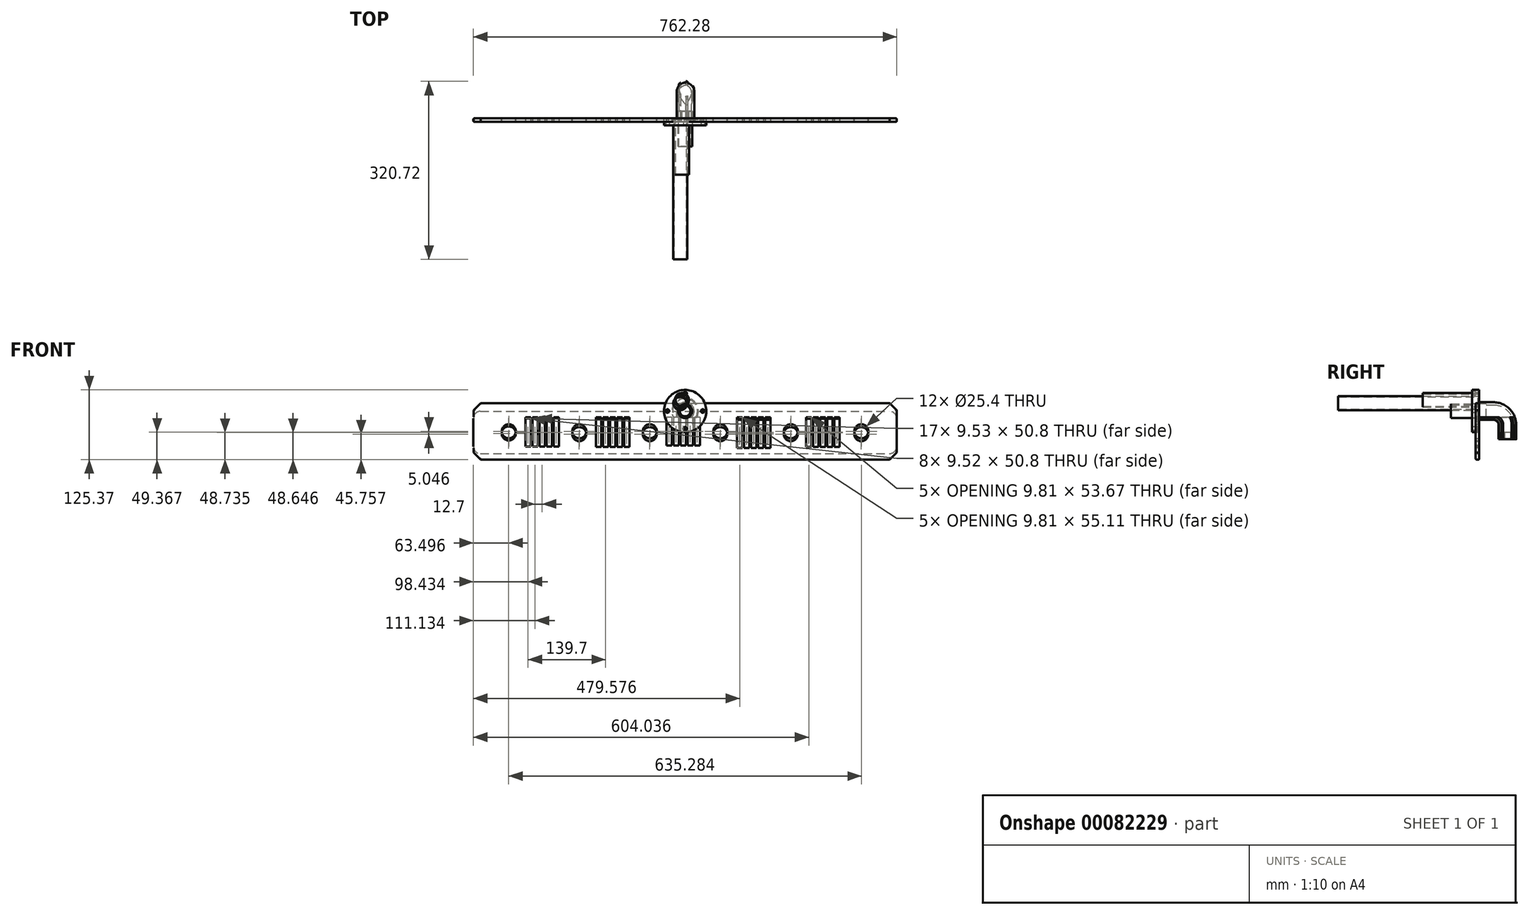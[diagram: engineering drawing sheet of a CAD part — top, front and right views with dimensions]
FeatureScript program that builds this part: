
annotation { "Feature Type Name" : "Feature", "Feature Type Description" : "" }
export const myFeature = defineFeature(function(context is Context, id is Id, definition is map)
    precondition{}
    {
        {
            var Q0;
            Q0=qCreatedBy(makeId("Front.planeOp"),FACE);
            var sketch = newSketch(context, id + "F0", { "sketchPlane" : qUnion([Q0])});
            skCircle(sketch, "E0", {"center": v(0, 0) * mm, "radius": 38.1 * mm});
            skCircle(sketch, "E1", {"center": v(0, 0) * mm, "radius": 9.53 * mm});
            skSolve(sketch);
        }
        {
            var Q0;
            Q0=makeQuery(id+"F0.imprint","IMPRINT",FACE,{"disambiguationData":[TD([[makeQuery(id+"F0.imprint","IMPRINT",EDGE,{"derivedFrom":sQuery(id+"F0.wireOp",EDGE,"E0")}),1.0]])]});
            extrude(context, id + "F1", {"entities" : qUnion([Q0]), "depth" : 12.7 * mm});
        }
        {
            var Q0;
            Q0=makeQuery(id+"F1.opExtrude","CAP_FACE",FACE,{"disambiguationData":[OSD([sQuery(id+"F0.wireOp",EDGE,"E0"),sQuery(id+"F0.wireOp",EDGE,"E1")])],"isStart":false});
            var sketch = newSketch(context, id + "F2", { "sketchPlane" : qUnion([Q0])});
            skCircle(sketch, "E2", {"center": v(0, 0) * mm, "radius": 12.7 * mm});
            skSolve(sketch);
        }
        {
            var Q0;
            Q0=makeQuery(id+"F2.imprint","IMPRINT",FACE,{"disambiguationData":[TD([[makeQuery(id+"F2.imprint","IMPRINT",EDGE,{"derivedFrom":sQuery(id+"F2.wireOp",EDGE,"E2")}),1.0]])]});
            extrude(context, id + "F3", {"entities" : qUnion([Q0]), "operationType" : NewBodyOperationType.REMOVE, "oppositeDirection" : true, "depth" : 6.35 * mm});
        }
        {
            var Q0;
            Q0=makeQuery(id+"F1.opExtrude","CAP_FACE",FACE,{"disambiguationData":[OSD([sQuery(id+"F0.wireOp",EDGE,"E0"),sQuery(id+"F0.wireOp",EDGE,"E1")])],"isStart":false});
            var sketch = newSketch(context, id + "F4", { "sketchPlane" : qUnion([Q0])});
            skPoint(sketch, "E3", {"position": v(0, 31.75) * mm});
            skPoint(sketch, "E4", {"position": v(31.75, 0) * mm});
            skPoint(sketch, "E5", {"position": v(0, -31.75) * mm});
            skPoint(sketch, "E6", {"position": v(-31.75, 0) * mm});
            skSolve(sketch);
        }
        {
            var Q0;
            Q0=sQuery(id+"F4.wireOp",VERTEX,"E3");
            var Q1;
            Q1=sQuery(id+"F4.wireOp",VERTEX,"E6");
            var Q2;
            Q2=sQuery(id+"F4.wireOp",VERTEX,"E4");
            var Q3;
            Q3=sQuery(id+"F4.wireOp",VERTEX,"E5");
            var Q4;
            Q4=makeQuery(id+"F1.opExtrude","SWEPT_BODY",BODY,{"disambiguationData":[OSD([sQuery(id+"F0.wireOp",EDGE,"E0"),sQuery(id+"F0.wireOp",EDGE,"E1")])]});
            hole(context, id + "F5", {"style" : HoleStyle.C_BORE, "endStyle" : HoleEndStyle.THROUGH, "holeDiameter" : 3.17 * mm, "cBoreDiameter" : 6.35 * mm, "cBoreDepth" : 6.35 * mm, "locations" : qUnion([Q0, Q1, Q2, Q3]), "scope" : qUnion([Q4]), "isTappedThrough" : true});
        }
        {
            var Q0;
            Q0=makeQuery(id+"F1.opExtrude","CAP_FACE",FACE,{"disambiguationData":[OSD([sQuery(id+"F0.wireOp",EDGE,"E0"),sQuery(id+"F0.wireOp",EDGE,"E1")])],"isStart":true});
            var sketch = newSketch(context, id + "F6", { "sketchPlane" : qUnion([Q0])});
            skCircle(sketch, "E7", {"center": v(0, 0) * mm, "radius": 22.23 * mm});
            skCircle(sketch, "E8", {"center": v(0, 0) * mm, "radius": 23.81 * mm});
            skSolve(sketch);
        }
        {
            var Q0;
            Q0=makeQuery(id+"F6.imprint","IMPRINT",FACE,{"disambiguationData":[TD([[makeQuery(id+"F6.imprint","IMPRINT",EDGE,{"derivedFrom":sQuery(id+"F6.wireOp",EDGE,"E7")}),-1.0]])]});
            extrude(context, id + "F7", {"entities" : qUnion([Q0]), "operationType" : NewBodyOperationType.REMOVE, "oppositeDirection" : true, "depth" : 1.9 * mm});
        }
        {
            var Q0;
            Q0=qCreatedBy(makeId("Front.planeOp"),FACE);
            var sketch = newSketch(context, id + "F8", { "sketchPlane" : qUnion([Q0])});
            skCircle(sketch, "E9", {"center": v(0, 0) * mm, "radius": 11.11 * mm});
            skCircle(sketch, "E10", {"center": v(0, 0) * mm, "radius": 12.7 * mm});
            skSolve(sketch);
        }
        {
            var Q0;
            Q0=makeQuery(id+"F8.imprint","IMPRINT",FACE,{"disambiguationData":[TD([[makeQuery(id+"F8.imprint","IMPRINT",EDGE,{"derivedFrom":sQuery(id+"F8.wireOp",EDGE,"E9")}),-1.0]])]});
            extrude(context, id + "F9", {"entities" : qUnion([Q0]), "depth" : 50.8 * mm});
        }
        {
            var Q0;
            Q0=qCreatedBy(makeId("Front.planeOp"),FACE);
            var sketch = newSketch(context, id + "F10", { "sketchPlane" : qUnion([Q0])});
            skCircle(sketch, "E11", {"center": v(-5.87, 19.79) * mm, "radius": 11.11 * mm});
            skCircle(sketch, "E12", {"center": v(-5.87, 19.79) * mm, "radius": 12.7 * mm});
            skSolve(sketch);
        }
        {
            var Q0;
            Q0=makeQuery(id+"F10.imprint","IMPRINT",FACE,{"disambiguationData":[TD([[makeQuery(id+"F10.imprint","IMPRINT",EDGE,{"derivedFrom":sQuery(id+"F10.wireOp",EDGE,"E11")}),-1.0]])]});
            extrude(context, id + "F11", {"entities" : qUnion([Q0]), "depth" : 101.6 * mm});
        }
        {
            var Q0;
            Q0=qCreatedBy(makeId("Front.planeOp"),FACE);
            var sketch = newSketch(context, id + "F12", { "sketchPlane" : qUnion([Q0])});
            skCircle(sketch, "E13", {"center": v(-8.71, 14.3) * mm, "radius": 11.11 * mm});
            skCircle(sketch, "E14", {"center": v(-8.71, 14.3) * mm, "radius": 12.7 * mm});
            skSolve(sketch);
        }
        {
            var Q0;
            Q0=makeQuery(id+"F12.imprint","IMPRINT",FACE,{"disambiguationData":[TD([[makeQuery(id+"F12.imprint","IMPRINT",EDGE,{"derivedFrom":sQuery(id+"F12.wireOp",EDGE,"E13")}),-1.0]])]});
            extrude(context, id + "F13", {"entities" : qUnion([Q0]), "depth" : 254 * mm});
        }
        {
            var Q0;
            Q0=qCreatedBy(makeId("Front.planeOp"),FACE);
            var sketch = newSketch(context, id + "F14", { "sketchPlane" : qUnion([Q0])});
            skCircle(sketch, "E15", {"center": v(0.38, 0.1) * mm, "radius": 11.11 * mm});
            skCircle(sketch, "E16", {"center": v(0.38, 0.1) * mm, "radius": 15.88 * mm});
            skSolve(sketch);
        }
        {
            var Q0;
            Q0=qCreatedBy(makeId("Right.planeOp"),FACE);
            var sketch = newSketch(context, id + "F15", { "sketchPlane" : qUnion([Q0])});
            skLineSegment(sketch, "E17", {"start": v(0, 0) * mm, "end": v(25.4, 0) * mm});
            skLineSegment(sketch, "E18", {"start": v(50.8, -25.4) * mm, "end": v(50.8, -50.8) * mm});
            skPoint(sketch, "E19.visualSharp", {"position": v(50.8, 0) * mm});
            skArc(sketch, "E19.filletArc", {"start": v(50.8, -25.4) * mm, "mid": v(43.36, -7.44) * mm, "end": v(25.4, 0) * mm});
            skSolve(sketch);
        }
        {
            var Q0;
            Q0=makeQuery(id+"F14.imprint","IMPRINT",FACE,{"disambiguationData":[TD([[makeQuery(id+"F14.imprint","IMPRINT",EDGE,{"derivedFrom":sQuery(id+"F14.wireOp",EDGE,"E15")}),-1.0]])]});
            var Q1;
            Q1=sQuery(id+"F15.wireOp",EDGE,"E19.filletArc");
            var Q2;
            Q2=sQuery(id+"F15.wireOp",EDGE,"E17");
            var Q3;
            Q3=sQuery(id+"F15.wireOp",EDGE,"E18");
            sweep(context, id + "F16", {"profiles" : qUnion([Q0]), "path" : qUnion([Q1, Q2, Q3])});
        }
        {
            var Q0;
            Q0=qCreatedBy(makeId("Front.planeOp"),FACE);
            var sketch = newSketch(context, id + "F17", { "sketchPlane" : qUnion([Q0])});
            skCircle(sketch, "E20", {"center": v(0, 0) * mm, "radius": 12.7 * mm});
            skSolve(sketch);
        }
        {
            var Q0;
            Q0=makeQuery(id+"F17.imprint","IMPRINT",FACE,{"disambiguationData":[TD([[makeQuery(id+"F17.imprint","IMPRINT",EDGE,{"derivedFrom":sQuery(id+"F17.wireOp",EDGE,"E20")}),1.0]])]});
            extrude(context, id + "F18", {"entities" : qUnion([Q0]), "operationType" : NewBodyOperationType.REMOVE, "oppositeDirection" : true, "depth" : 12.7 * mm});
        }
        {
            var Q0;
            Q0=makeQuery(id+"F16.opSweep","CAP_FACE",FACE,{"disambiguationData":[OSD([sQuery(id+"F14.wireOp",EDGE,"E15"),sQuery(id+"F14.wireOp",EDGE,"E16"),sQuery(id+"F15.wireOp",VERTEX,"E18.end")])],"isStart":false});
            var sketch = newSketch(context, id + "F19", { "sketchPlane" : qUnion([Q0])});
            skCircle(sketch, "E21", {"center": v(0.38, -50.9) * mm, "radius": 12.7 * mm});
            skSolve(sketch);
        }
        {
            var Q0;
            Q0 = qSketchRegion(id + "F19", true);
            extrude(context, id + "F20", {"entities" : qUnion([Q0]), "operationType" : NewBodyOperationType.REMOVE, "oppositeDirection" : true, "depth" : 12.7 * mm});
        }
        {
            var Q0;
            Q0=qCreatedBy(makeId("Front.planeOp"),FACE);
            var sketch = newSketch(context, id + "F21", { "sketchPlane" : qUnion([Q0])});
            skLineSegment(sketch, "E22.bottom", {"start": v(-381, 14.33) * mm, "end": v(381, 14.33) * mm});
            skLineSegment(sketch, "E22.top", {"start": v(-381, -87.27) * mm, "end": v(381, -87.27) * mm});
            skLineSegment(sketch, "E22.left", {"start": v(-381, 14.33) * mm, "end": v(-381, -87.27) * mm});
            skLineSegment(sketch, "E22.right", {"start": v(381, 14.33) * mm, "end": v(381, -87.27) * mm});
            skCircle(sketch, "E23", {"center": v(-317.5, -36.47) * mm, "radius": 12.7 * mm});
            skPoint(sketch, "E23.centerSnap0", {"position": v(-381, -36.47) * mm});
            skCircle(sketch, "E24", {"center": v(-190.5, -36.47) * mm, "radius": 12.7 * mm});
            skCircle(sketch, "E25", {"center": v(-63.5, -36.47) * mm, "radius": 12.7 * mm});
            skCircle(sketch, "E26", {"center": v(63.5, -36.47) * mm, "radius": 12.7 * mm});
            skCircle(sketch, "E27", {"center": v(190.5, -36.47) * mm, "radius": 12.7 * mm});
            skCircle(sketch, "E28", {"center": v(317.5, -36.47) * mm, "radius": 12.7 * mm});
            skSolve(sketch);
        }
        {
            var Q0;
            Q0=makeQuery(id+"F21.imprint","IMPRINT",FACE,{"disambiguationData":[TD([[makeQuery(id+"F21.imprint","IMPRINT",EDGE,{"derivedFrom":sQuery(id+"F21.wireOp",EDGE,"E22.bottom")}),-1.0]])]});
            extrude(context, id + "F22", {"entities" : qUnion([Q0]), "depth" : 6.35 * mm});
        }
        {
            var Q0;
            Q0=makeQuery(id+"F22.opExtrude","CAP_FACE",FACE,{"disambiguationData":[OSD([sQuery(id+"F21.wireOp",EDGE,"E22.bottom"),sQuery(id+"F21.wireOp",EDGE,"E22.top"),sQuery(id+"F21.wireOp",EDGE,"E22.left"),sQuery(id+"F21.wireOp",EDGE,"E22.right"),sQuery(id+"F21.wireOp",EDGE,"E23"),sQuery(id+"F21.wireOp",EDGE,"E24"),sQuery(id+"F21.wireOp",EDGE,"E25"),sQuery(id+"F21.wireOp",EDGE,"E26"),sQuery(id+"F21.wireOp",EDGE,"E27"),sQuery(id+"F21.wireOp",EDGE,"E28")])],"isStart":false});
            var sketch = newSketch(context, id + "F23", { "sketchPlane" : qUnion([Q0])});
            skLineSegment(sketch, "E29.bottom", {"start": v(-287.32, -11.07) * mm, "end": v(-277.8, -11.07) * mm});
            skLineSegment(sketch, "E29.top", {"start": v(-287.32, -61.87) * mm, "end": v(-277.8, -61.87) * mm});
            skLineSegment(sketch, "E29.left", {"start": v(-287.32, -11.07) * mm, "end": v(-287.32, -61.87) * mm});
            skLineSegment(sketch, "E29.right", {"start": v(-277.8, -11.07) * mm, "end": v(-277.8, -61.87) * mm});
            skLineSegment(sketch, "E30.1.0.0", {"start": v(-274.62, -11.07) * mm, "end": v(-265.1, -11.07) * mm});
            skLineSegment(sketch, "E30.1.0.1", {"start": v(-274.62, -61.87) * mm, "end": v(-265.1, -61.87) * mm});
            skLineSegment(sketch, "E30.1.0.2", {"start": v(-265.1, -11.07) * mm, "end": v(-265.1, -61.87) * mm});
            skLineSegment(sketch, "E30.1.0.3", {"start": v(-274.62, -11.07) * mm, "end": v(-274.62, -61.87) * mm});
            skLineSegment(sketch, "E30.2.0.0", {"start": v(-261.92, -11.07) * mm, "end": v(-252.4, -11.07) * mm});
            skLineSegment(sketch, "E30.2.0.1", {"start": v(-261.92, -61.87) * mm, "end": v(-252.4, -61.87) * mm});
            skLineSegment(sketch, "E30.2.0.2", {"start": v(-252.4, -11.07) * mm, "end": v(-252.4, -61.87) * mm});
            skLineSegment(sketch, "E30.2.0.3", {"start": v(-261.92, -11.07) * mm, "end": v(-261.92, -61.87) * mm});
            skLineSegment(sketch, "E30.3.0.0", {"start": v(-249.22, -11.07) * mm, "end": v(-239.7, -11.07) * mm});
            skLineSegment(sketch, "E30.3.0.1", {"start": v(-249.22, -61.87) * mm, "end": v(-239.7, -61.87) * mm});
            skLineSegment(sketch, "E30.3.0.2", {"start": v(-239.7, -11.07) * mm, "end": v(-239.7, -61.87) * mm});
            skLineSegment(sketch, "E30.3.0.3", {"start": v(-249.22, -11.07) * mm, "end": v(-249.22, -61.87) * mm});
            skLineSegment(sketch, "E30.4.0.0", {"start": v(-236.52, -11.07) * mm, "end": v(-227, -11.07) * mm});
            skLineSegment(sketch, "E30.4.0.1", {"start": v(-236.52, -61.87) * mm, "end": v(-227, -61.87) * mm});
            skLineSegment(sketch, "E30.4.0.2", {"start": v(-227, -11.07) * mm, "end": v(-227, -61.87) * mm});
            skLineSegment(sketch, "E30.4.0.3", {"start": v(-236.52, -11.07) * mm, "end": v(-236.52, -61.87) * mm});
            skLineSegment(sketch, "E30.direction1", {"start": v(-287.32, -11.07) * mm, "end": v(-274.62, -11.07) * mm, "construction": true});
            skLineSegment(sketch, "E31.bottom", {"start": v(-160.32, -11.07) * mm, "end": v(-150.8, -11.07) * mm});
            skLineSegment(sketch, "E31.top", {"start": v(-160.32, -61.87) * mm, "end": v(-150.8, -61.87) * mm});
            skLineSegment(sketch, "E31.left", {"start": v(-160.32, -11.07) * mm, "end": v(-160.32, -61.87) * mm});
            skLineSegment(sketch, "E31.right", {"start": v(-150.8, -11.07) * mm, "end": v(-150.8, -61.87) * mm});
            skLineSegment(sketch, "E32.1.0.0", {"start": v(-147.62, -11.07) * mm, "end": v(-138.1, -11.07) * mm});
            skLineSegment(sketch, "E32.1.0.1", {"start": v(-147.62, -61.87) * mm, "end": v(-138.1, -61.87) * mm});
            skLineSegment(sketch, "E32.1.0.2", {"start": v(-138.1, -11.07) * mm, "end": v(-138.1, -61.87) * mm});
            skLineSegment(sketch, "E32.1.0.3", {"start": v(-147.62, -11.07) * mm, "end": v(-147.62, -61.87) * mm});
            skLineSegment(sketch, "E32.2.0.0", {"start": v(-134.92, -11.07) * mm, "end": v(-125.4, -11.07) * mm});
            skLineSegment(sketch, "E32.2.0.1", {"start": v(-134.92, -61.87) * mm, "end": v(-125.4, -61.87) * mm});
            skLineSegment(sketch, "E32.2.0.2", {"start": v(-125.4, -11.07) * mm, "end": v(-125.4, -61.87) * mm});
            skLineSegment(sketch, "E32.2.0.3", {"start": v(-134.92, -11.07) * mm, "end": v(-134.92, -61.87) * mm});
            skLineSegment(sketch, "E32.3.0.0", {"start": v(-122.22, -11.07) * mm, "end": v(-112.7, -11.07) * mm});
            skLineSegment(sketch, "E32.3.0.1", {"start": v(-122.22, -61.87) * mm, "end": v(-112.7, -61.87) * mm});
            skLineSegment(sketch, "E32.3.0.2", {"start": v(-112.7, -11.07) * mm, "end": v(-112.7, -61.87) * mm});
            skLineSegment(sketch, "E32.3.0.3", {"start": v(-122.22, -11.07) * mm, "end": v(-122.22, -61.87) * mm});
            skLineSegment(sketch, "E32.4.0.0", {"start": v(-109.52, -11.07) * mm, "end": v(-100, -11.07) * mm});
            skLineSegment(sketch, "E32.4.0.1", {"start": v(-109.52, -61.87) * mm, "end": v(-100, -61.87) * mm});
            skLineSegment(sketch, "E32.4.0.2", {"start": v(-100, -11.07) * mm, "end": v(-100, -61.87) * mm});
            skLineSegment(sketch, "E32.4.0.3", {"start": v(-109.52, -11.07) * mm, "end": v(-109.52, -61.87) * mm});
            skLineSegment(sketch, "E32.direction1", {"start": v(-160.32, -11.07) * mm, "end": v(-147.62, -11.07) * mm, "construction": true});
            skLineSegment(sketch, "E33.bottom", {"start": v(-33.32, -11.07) * mm, "end": v(-23.8, -11.07) * mm});
            skLineSegment(sketch, "E33.top", {"start": v(-33.32, -61.87) * mm, "end": v(-23.8, -61.87) * mm});
            skLineSegment(sketch, "E33.left", {"start": v(-33.32, -11.07) * mm, "end": v(-33.32, -61.87) * mm});
            skLineSegment(sketch, "E33.right", {"start": v(-23.8, -11.07) * mm, "end": v(-23.8, -61.87) * mm});
            skLineSegment(sketch, "E34.1.0.0", {"start": v(-20.62, -11.07) * mm, "end": v(-11.1, -11.07) * mm});
            skLineSegment(sketch, "E34.1.0.1", {"start": v(-20.62, -61.87) * mm, "end": v(-11.1, -61.87) * mm});
            skLineSegment(sketch, "E34.1.0.2", {"start": v(-11.1, -11.07) * mm, "end": v(-11.1, -61.87) * mm});
            skLineSegment(sketch, "E34.1.0.3", {"start": v(-20.62, -11.07) * mm, "end": v(-20.62, -61.87) * mm});
            skLineSegment(sketch, "E34.2.0.0", {"start": v(-7.92, -11.07) * mm, "end": v(1.6, -11.07) * mm});
            skLineSegment(sketch, "E34.2.0.1", {"start": v(-7.92, -61.87) * mm, "end": v(1.6, -61.87) * mm});
            skLineSegment(sketch, "E34.2.0.2", {"start": v(1.6, -11.07) * mm, "end": v(1.6, -61.87) * mm});
            skLineSegment(sketch, "E34.2.0.3", {"start": v(-7.92, -11.07) * mm, "end": v(-7.92, -61.87) * mm});
            skLineSegment(sketch, "E34.3.0.0", {"start": v(4.78, -11.07) * mm, "end": v(14.3, -11.07) * mm});
            skLineSegment(sketch, "E34.3.0.1", {"start": v(4.78, -61.87) * mm, "end": v(14.3, -61.87) * mm});
            skLineSegment(sketch, "E34.3.0.2", {"start": v(14.3, -11.07) * mm, "end": v(14.3, -61.87) * mm});
            skLineSegment(sketch, "E34.3.0.3", {"start": v(4.78, -11.07) * mm, "end": v(4.78, -61.87) * mm});
            skLineSegment(sketch, "E34.4.0.0", {"start": v(17.48, -11.07) * mm, "end": v(27, -11.07) * mm});
            skLineSegment(sketch, "E34.4.0.1", {"start": v(17.48, -61.87) * mm, "end": v(27, -61.87) * mm});
            skLineSegment(sketch, "E34.4.0.2", {"start": v(27, -11.07) * mm, "end": v(27, -61.87) * mm});
            skLineSegment(sketch, "E34.4.0.3", {"start": v(17.48, -11.07) * mm, "end": v(17.48, -61.87) * mm});
            skLineSegment(sketch, "E34.direction1", {"start": v(-33.32, -11.07) * mm, "end": v(-20.62, -11.07) * mm, "construction": true});
            skLineSegment(sketch, "E35.bottom", {"start": v(93.68, -11.07) * mm, "end": v(103.2, -11.07) * mm});
            skLineSegment(sketch, "E35.top", {"start": v(93.68, -61.87) * mm, "end": v(103.2, -61.87) * mm});
            skLineSegment(sketch, "E35.left", {"start": v(93.68, -11.07) * mm, "end": v(93.68, -61.87) * mm});
            skLineSegment(sketch, "E35.right", {"start": v(103.2, -11.07) * mm, "end": v(103.2, -61.87) * mm});
            skLineSegment(sketch, "E36.1.0.0", {"start": v(106.38, -11.07) * mm, "end": v(115.9, -11.07) * mm});
            skLineSegment(sketch, "E36.1.0.1", {"start": v(106.38, -61.87) * mm, "end": v(115.9, -61.87) * mm});
            skLineSegment(sketch, "E36.1.0.2", {"start": v(115.9, -11.07) * mm, "end": v(115.9, -61.87) * mm});
            skLineSegment(sketch, "E36.1.0.3", {"start": v(106.38, -11.07) * mm, "end": v(106.38, -61.87) * mm});
            skLineSegment(sketch, "E36.2.0.0", {"start": v(119.08, -11.07) * mm, "end": v(128.6, -11.07) * mm});
            skLineSegment(sketch, "E36.2.0.1", {"start": v(119.08, -61.87) * mm, "end": v(128.6, -61.87) * mm});
            skLineSegment(sketch, "E36.2.0.2", {"start": v(128.6, -11.07) * mm, "end": v(128.6, -61.87) * mm});
            skLineSegment(sketch, "E36.2.0.3", {"start": v(119.08, -11.07) * mm, "end": v(119.08, -61.87) * mm});
            skLineSegment(sketch, "E36.3.0.0", {"start": v(131.78, -11.07) * mm, "end": v(141.3, -11.07) * mm});
            skLineSegment(sketch, "E36.3.0.1", {"start": v(131.78, -61.87) * mm, "end": v(141.3, -61.87) * mm});
            skLineSegment(sketch, "E36.3.0.2", {"start": v(141.3, -11.07) * mm, "end": v(141.3, -61.87) * mm});
            skLineSegment(sketch, "E36.3.0.3", {"start": v(131.78, -11.07) * mm, "end": v(131.78, -61.87) * mm});
            skLineSegment(sketch, "E36.4.0.0", {"start": v(144.48, -11.07) * mm, "end": v(154, -11.07) * mm});
            skLineSegment(sketch, "E36.4.0.1", {"start": v(144.48, -61.87) * mm, "end": v(154, -61.87) * mm});
            skLineSegment(sketch, "E36.4.0.2", {"start": v(154, -11.07) * mm, "end": v(154, -61.87) * mm});
            skLineSegment(sketch, "E36.4.0.3", {"start": v(144.48, -11.07) * mm, "end": v(144.48, -61.87) * mm});
            skLineSegment(sketch, "E36.direction1", {"start": v(93.68, -11.07) * mm, "end": v(106.38, -11.07) * mm, "construction": true});
            skLineSegment(sketch, "E37.bottom", {"start": v(218.14, -11.07) * mm, "end": v(227.66, -11.07) * mm});
            skLineSegment(sketch, "E37.top", {"start": v(218.14, -61.87) * mm, "end": v(227.66, -61.87) * mm});
            skLineSegment(sketch, "E37.left", {"start": v(218.14, -11.07) * mm, "end": v(218.14, -61.87) * mm});
            skLineSegment(sketch, "E37.right", {"start": v(227.66, -11.07) * mm, "end": v(227.66, -61.87) * mm});
            skLineSegment(sketch, "E38.1.0.0", {"start": v(230.84, -11.07) * mm, "end": v(240.36, -11.07) * mm});
            skLineSegment(sketch, "E38.1.0.1", {"start": v(230.84, -61.87) * mm, "end": v(240.36, -61.87) * mm});
            skLineSegment(sketch, "E38.1.0.2", {"start": v(240.36, -11.07) * mm, "end": v(240.36, -61.87) * mm});
            skLineSegment(sketch, "E38.1.0.3", {"start": v(230.84, -11.07) * mm, "end": v(230.84, -61.87) * mm});
            skLineSegment(sketch, "E38.2.0.0", {"start": v(243.54, -11.07) * mm, "end": v(253.06, -11.07) * mm});
            skLineSegment(sketch, "E38.2.0.1", {"start": v(243.54, -61.87) * mm, "end": v(253.06, -61.87) * mm});
            skLineSegment(sketch, "E38.2.0.2", {"start": v(253.06, -11.07) * mm, "end": v(253.06, -61.87) * mm});
            skLineSegment(sketch, "E38.2.0.3", {"start": v(243.54, -11.07) * mm, "end": v(243.54, -61.87) * mm});
            skLineSegment(sketch, "E38.3.0.0", {"start": v(256.24, -11.07) * mm, "end": v(265.76, -11.07) * mm});
            skLineSegment(sketch, "E38.3.0.1", {"start": v(256.24, -61.87) * mm, "end": v(265.76, -61.87) * mm});
            skLineSegment(sketch, "E38.3.0.2", {"start": v(265.76, -11.07) * mm, "end": v(265.76, -61.87) * mm});
            skLineSegment(sketch, "E38.3.0.3", {"start": v(256.24, -11.07) * mm, "end": v(256.24, -61.87) * mm});
            skLineSegment(sketch, "E38.4.0.0", {"start": v(268.94, -11.07) * mm, "end": v(278.46, -11.07) * mm});
            skLineSegment(sketch, "E38.4.0.1", {"start": v(268.94, -61.87) * mm, "end": v(278.46, -61.87) * mm});
            skLineSegment(sketch, "E38.4.0.2", {"start": v(278.46, -11.07) * mm, "end": v(278.46, -61.87) * mm});
            skLineSegment(sketch, "E38.4.0.3", {"start": v(268.94, -11.07) * mm, "end": v(268.94, -61.87) * mm});
            skLineSegment(sketch, "E38.direction1", {"start": v(218.14, -11.07) * mm, "end": v(230.84, -11.07) * mm, "construction": true});
            skSolve(sketch);
        }
        {
            var Q0;
            Q0 = qSketchRegion(id + "F23", true);
            extrude(context, id + "F24", {"entities" : qUnion([Q0]), "operationType" : NewBodyOperationType.REMOVE, "endBound" : BoundingType.THROUGH_ALL, "oppositeDirection" : true, "depth" : 25.4 * mm});
        }
        {
            var Q0;
            Q0=makeQuery(id+"F22.opExtrude","SWEPT_EDGE",EDGE,{"disambiguationData":[OSD([sQuery(id+"F21.wireOp",EDGE,"E22.bottom"),sQuery(id+"F21.wireOp",EDGE,"E22.left")])]});
            var Q1;
            Q1=makeQuery(id+"F22.opExtrude","SWEPT_EDGE",EDGE,{"disambiguationData":[OSD([sQuery(id+"F21.wireOp",EDGE,"E22.top"),sQuery(id+"F21.wireOp",EDGE,"E22.left")])]});
            var Q2;
            Q2=makeQuery(id+"F22.opExtrude","SWEPT_EDGE",EDGE,{"disambiguationData":[OSD([sQuery(id+"F21.wireOp",EDGE,"E22.bottom"),sQuery(id+"F21.wireOp",EDGE,"E22.right")])]});
            var Q3;
            Q3=makeQuery(id+"F22.opExtrude","SWEPT_EDGE",EDGE,{"disambiguationData":[OSD([sQuery(id+"F21.wireOp",EDGE,"E22.top"),sQuery(id+"F21.wireOp",EDGE,"E22.right")])]});
            chamfer(context, id + "F25", {"entities" : qUnion([Q0, Q1, Q2, Q3]), "width" : 12.7 * mm, "tangentPropagation" : true});
        }
        {
            var Q0;
            {var subQ0=sQuery(id+"F21.wireOp",EDGE,"E22.left");var subQ1=sQuery(id+"F21.wireOp",EDGE,"E22.bottom");Q0=makeQuery(id+"F25.opChamfer","BLEND_EDGE",EDGE,{"blendedFrom":[makeQuery(id+"F22.opExtrude","SWEPT_EDGE",EDGE,{"disambiguationData":[OSD([subQ1,subQ0])]}),makeQuery(id+"F22.opExtrude","CAP_FACE",FACE,{"disambiguationData":[OSD([subQ1,sQuery(id+"F21.wireOp",EDGE,"E22.top"),subQ0,sQuery(id+"F21.wireOp",EDGE,"E22.right"),sQuery(id+"F21.wireOp",EDGE,"E23"),sQuery(id+"F21.wireOp",EDGE,"E24"),sQuery(id+"F21.wireOp",EDGE,"E25"),sQuery(id+"F21.wireOp",EDGE,"E26"),sQuery(id+"F21.wireOp",EDGE,"E27"),sQuery(id+"F21.wireOp",EDGE,"E28")])],"isStart":false})],"blendedInto":[makeQuery(id+"F22.opExtrude","CAP_FACE",FACE,{"disambiguationData":[OSD([subQ1,sQuery(id+"F21.wireOp",EDGE,"E22.top"),subQ0,sQuery(id+"F21.wireOp",EDGE,"E22.right"),sQuery(id+"F21.wireOp",EDGE,"E23"),sQuery(id+"F21.wireOp",EDGE,"E24"),sQuery(id+"F21.wireOp",EDGE,"E25"),sQuery(id+"F21.wireOp",EDGE,"E26"),sQuery(id+"F21.wireOp",EDGE,"E27"),sQuery(id+"F21.wireOp",EDGE,"E28")])],"isStart":false})]});}
            var Q1;
            {var subQ0=sQuery(id+"F21.wireOp",EDGE,"E22.left");var subQ1=sQuery(id+"F21.wireOp",EDGE,"E22.top");Q1=makeQuery(id+"F25.opChamfer","BLEND_EDGE",EDGE,{"blendedFrom":[makeQuery(id+"F22.opExtrude","SWEPT_EDGE",EDGE,{"disambiguationData":[OSD([subQ1,subQ0])]}),makeQuery(id+"F22.opExtrude","CAP_FACE",FACE,{"disambiguationData":[OSD([sQuery(id+"F21.wireOp",EDGE,"E22.bottom"),subQ1,subQ0,sQuery(id+"F21.wireOp",EDGE,"E22.right"),sQuery(id+"F21.wireOp",EDGE,"E23"),sQuery(id+"F21.wireOp",EDGE,"E24"),sQuery(id+"F21.wireOp",EDGE,"E25"),sQuery(id+"F21.wireOp",EDGE,"E26"),sQuery(id+"F21.wireOp",EDGE,"E27"),sQuery(id+"F21.wireOp",EDGE,"E28")])],"isStart":false})],"blendedInto":[makeQuery(id+"F22.opExtrude","CAP_FACE",FACE,{"disambiguationData":[OSD([sQuery(id+"F21.wireOp",EDGE,"E22.bottom"),subQ1,subQ0,sQuery(id+"F21.wireOp",EDGE,"E22.right"),sQuery(id+"F21.wireOp",EDGE,"E23"),sQuery(id+"F21.wireOp",EDGE,"E24"),sQuery(id+"F21.wireOp",EDGE,"E25"),sQuery(id+"F21.wireOp",EDGE,"E26"),sQuery(id+"F21.wireOp",EDGE,"E27"),sQuery(id+"F21.wireOp",EDGE,"E28")])],"isStart":false})]});}
            var Q2;
            {var subQ0=sQuery(id+"F21.wireOp",EDGE,"E22.right");var subQ1=sQuery(id+"F21.wireOp",EDGE,"E22.bottom");Q2=makeQuery(id+"F25.opChamfer","BLEND_EDGE",EDGE,{"blendedFrom":[makeQuery(id+"F22.opExtrude","SWEPT_EDGE",EDGE,{"disambiguationData":[OSD([subQ1,subQ0])]}),makeQuery(id+"F22.opExtrude","CAP_FACE",FACE,{"disambiguationData":[OSD([subQ1,sQuery(id+"F21.wireOp",EDGE,"E22.top"),sQuery(id+"F21.wireOp",EDGE,"E22.left"),subQ0,sQuery(id+"F21.wireOp",EDGE,"E23"),sQuery(id+"F21.wireOp",EDGE,"E24"),sQuery(id+"F21.wireOp",EDGE,"E25"),sQuery(id+"F21.wireOp",EDGE,"E26"),sQuery(id+"F21.wireOp",EDGE,"E27"),sQuery(id+"F21.wireOp",EDGE,"E28")])],"isStart":false})],"blendedInto":[makeQuery(id+"F22.opExtrude","CAP_FACE",FACE,{"disambiguationData":[OSD([subQ1,sQuery(id+"F21.wireOp",EDGE,"E22.top"),sQuery(id+"F21.wireOp",EDGE,"E22.left"),subQ0,sQuery(id+"F21.wireOp",EDGE,"E23"),sQuery(id+"F21.wireOp",EDGE,"E24"),sQuery(id+"F21.wireOp",EDGE,"E25"),sQuery(id+"F21.wireOp",EDGE,"E26"),sQuery(id+"F21.wireOp",EDGE,"E27"),sQuery(id+"F21.wireOp",EDGE,"E28")])],"isStart":false})]});}
            var Q3;
            {var subQ0=sQuery(id+"F21.wireOp",EDGE,"E22.right");var subQ1=sQuery(id+"F21.wireOp",EDGE,"E22.top");Q3=makeQuery(id+"F25.opChamfer","BLEND_EDGE",EDGE,{"blendedFrom":[makeQuery(id+"F22.opExtrude","SWEPT_EDGE",EDGE,{"disambiguationData":[OSD([subQ1,subQ0])]}),makeQuery(id+"F22.opExtrude","CAP_FACE",FACE,{"disambiguationData":[OSD([sQuery(id+"F21.wireOp",EDGE,"E22.bottom"),subQ1,sQuery(id+"F21.wireOp",EDGE,"E22.left"),subQ0,sQuery(id+"F21.wireOp",EDGE,"E23"),sQuery(id+"F21.wireOp",EDGE,"E24"),sQuery(id+"F21.wireOp",EDGE,"E25"),sQuery(id+"F21.wireOp",EDGE,"E26"),sQuery(id+"F21.wireOp",EDGE,"E27"),sQuery(id+"F21.wireOp",EDGE,"E28")])],"isStart":false})],"blendedInto":[makeQuery(id+"F22.opExtrude","CAP_FACE",FACE,{"disambiguationData":[OSD([sQuery(id+"F21.wireOp",EDGE,"E22.bottom"),subQ1,sQuery(id+"F21.wireOp",EDGE,"E22.left"),subQ0,sQuery(id+"F21.wireOp",EDGE,"E23"),sQuery(id+"F21.wireOp",EDGE,"E24"),sQuery(id+"F21.wireOp",EDGE,"E25"),sQuery(id+"F21.wireOp",EDGE,"E26"),sQuery(id+"F21.wireOp",EDGE,"E27"),sQuery(id+"F21.wireOp",EDGE,"E28")])],"isStart":false})]});}
            var Q4;
            Q4=makeQuery(id+"F22.opExtrude","CAP_EDGE",EDGE,{"disambiguationData":[OSD([sQuery(id+"F21.wireOp",EDGE,"E22.bottom")])],"isStart":false});
            var Q5;
            Q5=makeQuery(id+"F22.opExtrude","CAP_EDGE",EDGE,{"disambiguationData":[OSD([sQuery(id+"F21.wireOp",EDGE,"E22.top")])],"isStart":false});
            var Q6;
            Q6=makeQuery(id+"F22.opExtrude","CAP_EDGE",EDGE,{"disambiguationData":[OSD([sQuery(id+"F21.wireOp",EDGE,"E22.left")])],"isStart":false});
            var Q7;
            Q7=makeQuery(id+"F22.opExtrude","CAP_EDGE",EDGE,{"disambiguationData":[OSD([sQuery(id+"F21.wireOp",EDGE,"E22.right")])],"isStart":false});
            var Q8;
            Q8=makeQuery(id+"F22.opExtrude","CAP_EDGE",EDGE,{"disambiguationData":[OSD([sQuery(id+"F21.wireOp",EDGE,"E22.bottom")])],"isStart":true});
            var Q9;
            {var subQ0=sQuery(id+"F21.wireOp",EDGE,"E22.right");var subQ1=sQuery(id+"F21.wireOp",EDGE,"E22.bottom");Q9=makeQuery(id+"F25.opChamfer","BLEND_EDGE",EDGE,{"blendedFrom":[makeQuery(id+"F22.opExtrude","SWEPT_EDGE",EDGE,{"disambiguationData":[OSD([subQ1,subQ0])]}),makeQuery(id+"F22.opExtrude","CAP_FACE",FACE,{"disambiguationData":[OSD([subQ1,sQuery(id+"F21.wireOp",EDGE,"E22.top"),sQuery(id+"F21.wireOp",EDGE,"E22.left"),subQ0,sQuery(id+"F21.wireOp",EDGE,"E23"),sQuery(id+"F21.wireOp",EDGE,"E24"),sQuery(id+"F21.wireOp",EDGE,"E25"),sQuery(id+"F21.wireOp",EDGE,"E26"),sQuery(id+"F21.wireOp",EDGE,"E27"),sQuery(id+"F21.wireOp",EDGE,"E28")])],"isStart":true})],"blendedInto":[makeQuery(id+"F22.opExtrude","CAP_FACE",FACE,{"disambiguationData":[OSD([subQ1,sQuery(id+"F21.wireOp",EDGE,"E22.top"),sQuery(id+"F21.wireOp",EDGE,"E22.left"),subQ0,sQuery(id+"F21.wireOp",EDGE,"E23"),sQuery(id+"F21.wireOp",EDGE,"E24"),sQuery(id+"F21.wireOp",EDGE,"E25"),sQuery(id+"F21.wireOp",EDGE,"E26"),sQuery(id+"F21.wireOp",EDGE,"E27"),sQuery(id+"F21.wireOp",EDGE,"E28")])],"isStart":true})]});}
            var Q10;
            Q10=makeQuery(id+"F22.opExtrude","CAP_EDGE",EDGE,{"disambiguationData":[OSD([sQuery(id+"F21.wireOp",EDGE,"E22.right")])],"isStart":true});
            var Q11;
            {var subQ0=sQuery(id+"F21.wireOp",EDGE,"E22.right");var subQ1=sQuery(id+"F21.wireOp",EDGE,"E22.top");Q11=makeQuery(id+"F25.opChamfer","BLEND_EDGE",EDGE,{"blendedFrom":[makeQuery(id+"F22.opExtrude","SWEPT_EDGE",EDGE,{"disambiguationData":[OSD([subQ1,subQ0])]}),makeQuery(id+"F22.opExtrude","CAP_FACE",FACE,{"disambiguationData":[OSD([sQuery(id+"F21.wireOp",EDGE,"E22.bottom"),subQ1,sQuery(id+"F21.wireOp",EDGE,"E22.left"),subQ0,sQuery(id+"F21.wireOp",EDGE,"E23"),sQuery(id+"F21.wireOp",EDGE,"E24"),sQuery(id+"F21.wireOp",EDGE,"E25"),sQuery(id+"F21.wireOp",EDGE,"E26"),sQuery(id+"F21.wireOp",EDGE,"E27"),sQuery(id+"F21.wireOp",EDGE,"E28")])],"isStart":true})],"blendedInto":[makeQuery(id+"F22.opExtrude","CAP_FACE",FACE,{"disambiguationData":[OSD([sQuery(id+"F21.wireOp",EDGE,"E22.bottom"),subQ1,sQuery(id+"F21.wireOp",EDGE,"E22.left"),subQ0,sQuery(id+"F21.wireOp",EDGE,"E23"),sQuery(id+"F21.wireOp",EDGE,"E24"),sQuery(id+"F21.wireOp",EDGE,"E25"),sQuery(id+"F21.wireOp",EDGE,"E26"),sQuery(id+"F21.wireOp",EDGE,"E27"),sQuery(id+"F21.wireOp",EDGE,"E28")])],"isStart":true})]});}
            var Q12;
            Q12=makeQuery(id+"F22.opExtrude","CAP_EDGE",EDGE,{"disambiguationData":[OSD([sQuery(id+"F21.wireOp",EDGE,"E22.top")])],"isStart":true});
            var Q13;
            {var subQ0=sQuery(id+"F21.wireOp",EDGE,"E22.left");var subQ1=sQuery(id+"F21.wireOp",EDGE,"E22.bottom");Q13=makeQuery(id+"F25.opChamfer","BLEND_EDGE",EDGE,{"blendedFrom":[makeQuery(id+"F22.opExtrude","SWEPT_EDGE",EDGE,{"disambiguationData":[OSD([subQ1,subQ0])]}),makeQuery(id+"F22.opExtrude","CAP_FACE",FACE,{"disambiguationData":[OSD([subQ1,sQuery(id+"F21.wireOp",EDGE,"E22.top"),subQ0,sQuery(id+"F21.wireOp",EDGE,"E22.right"),sQuery(id+"F21.wireOp",EDGE,"E23"),sQuery(id+"F21.wireOp",EDGE,"E24"),sQuery(id+"F21.wireOp",EDGE,"E25"),sQuery(id+"F21.wireOp",EDGE,"E26"),sQuery(id+"F21.wireOp",EDGE,"E27"),sQuery(id+"F21.wireOp",EDGE,"E28")])],"isStart":true})],"blendedInto":[makeQuery(id+"F22.opExtrude","CAP_FACE",FACE,{"disambiguationData":[OSD([subQ1,sQuery(id+"F21.wireOp",EDGE,"E22.top"),subQ0,sQuery(id+"F21.wireOp",EDGE,"E22.right"),sQuery(id+"F21.wireOp",EDGE,"E23"),sQuery(id+"F21.wireOp",EDGE,"E24"),sQuery(id+"F21.wireOp",EDGE,"E25"),sQuery(id+"F21.wireOp",EDGE,"E26"),sQuery(id+"F21.wireOp",EDGE,"E27"),sQuery(id+"F21.wireOp",EDGE,"E28")])],"isStart":true})]});}
            var Q14;
            Q14=makeQuery(id+"F22.opExtrude","CAP_EDGE",EDGE,{"disambiguationData":[OSD([sQuery(id+"F21.wireOp",EDGE,"E22.left")])],"isStart":true});
            var Q15;
            {var subQ0=sQuery(id+"F21.wireOp",EDGE,"E22.left");var subQ1=sQuery(id+"F21.wireOp",EDGE,"E22.top");Q15=makeQuery(id+"F25.opChamfer","BLEND_EDGE",EDGE,{"blendedFrom":[makeQuery(id+"F22.opExtrude","SWEPT_EDGE",EDGE,{"disambiguationData":[OSD([subQ1,subQ0])]}),makeQuery(id+"F22.opExtrude","CAP_FACE",FACE,{"disambiguationData":[OSD([sQuery(id+"F21.wireOp",EDGE,"E22.bottom"),subQ1,subQ0,sQuery(id+"F21.wireOp",EDGE,"E22.right"),sQuery(id+"F21.wireOp",EDGE,"E23"),sQuery(id+"F21.wireOp",EDGE,"E24"),sQuery(id+"F21.wireOp",EDGE,"E25"),sQuery(id+"F21.wireOp",EDGE,"E26"),sQuery(id+"F21.wireOp",EDGE,"E27"),sQuery(id+"F21.wireOp",EDGE,"E28")])],"isStart":true})],"blendedInto":[makeQuery(id+"F22.opExtrude","CAP_FACE",FACE,{"disambiguationData":[OSD([sQuery(id+"F21.wireOp",EDGE,"E22.bottom"),subQ1,subQ0,sQuery(id+"F21.wireOp",EDGE,"E22.right"),sQuery(id+"F21.wireOp",EDGE,"E23"),sQuery(id+"F21.wireOp",EDGE,"E24"),sQuery(id+"F21.wireOp",EDGE,"E25"),sQuery(id+"F21.wireOp",EDGE,"E26"),sQuery(id+"F21.wireOp",EDGE,"E27"),sQuery(id+"F21.wireOp",EDGE,"E28")])],"isStart":true})]});}
            fillet(context, id + "F26", {"entities" : qUnion([Q0, Q1, Q2, Q3, Q4, Q5, Q6, Q7, Q8, Q9, Q10, Q11, Q12, Q13, Q14, Q15]), "radius" : 1.6 * mm, "tangentPropagation" : true, "allowEdgeOverflow" : false});
        }
        {
            var Q0;
            Q0=qCreatedBy(makeId("Front.planeOp"),FACE);
            var sketch = newSketch(context, id + "F27", { "sketchPlane" : qUnion([Q0])});
            skLineSegment(sketch, "E39.bottom", {"start": v(-381.28, -0.43) * mm, "end": v(380.72, -0.43) * mm});
            skLineSegment(sketch, "E39.top", {"start": v(-381.28, -76.63) * mm, "end": v(380.72, -76.63) * mm});
            skLineSegment(sketch, "E39.left", {"start": v(-381.28, -0.43) * mm, "end": v(-381.28, -76.63) * mm});
            skLineSegment(sketch, "E39.right", {"start": v(380.72, -0.43) * mm, "end": v(380.72, -76.63) * mm});
            skCircle(sketch, "E40", {"center": v(-317.78, -40.3) * mm, "radius": 12.7 * mm});
            skCircle(sketch, "E41", {"center": v(-190.78, -41.51) * mm, "radius": 12.7 * mm});
            skCircle(sketch, "E42", {"center": v(-63.78, -41.51) * mm, "radius": 12.7 * mm});
            skCircle(sketch, "E43", {"center": v(63.22, -41.51) * mm, "radius": 12.7 * mm});
            skCircle(sketch, "E44", {"center": v(190.22, -41.51) * mm, "radius": 12.7 * mm});
            skCircle(sketch, "E45", {"center": v(317.22, -41.51) * mm, "radius": 12.7 * mm});
            skSolve(sketch);
        }
        {
            var Q0;
            Q0=makeQuery(id+"F27.imprint","IMPRINT",FACE,{"disambiguationData":[TD([[makeQuery(id+"F27.imprint","IMPRINT",EDGE,{"derivedFrom":sQuery(id+"F27.wireOp",EDGE,"E39.bottom")}),-1.0]])]});
            extrude(context, id + "F28", {"entities" : qUnion([Q0]), "depth" : 6.35 * mm});
        }
        {
            var Q0;
            Q0=makeQuery(id+"F28.opExtrude","CAP_FACE",FACE,{"disambiguationData":[OSD([sQuery(id+"F27.wireOp",EDGE,"E39.bottom"),sQuery(id+"F27.wireOp",EDGE,"E39.top"),sQuery(id+"F27.wireOp",EDGE,"E39.left"),sQuery(id+"F27.wireOp",EDGE,"E39.right"),sQuery(id+"F27.wireOp",EDGE,"E40"),sQuery(id+"F27.wireOp",EDGE,"E41"),sQuery(id+"F27.wireOp",EDGE,"E42"),sQuery(id+"F27.wireOp",EDGE,"E43"),sQuery(id+"F27.wireOp",EDGE,"E44"),sQuery(id+"F27.wireOp",EDGE,"E45")])],"isStart":false});
            var sketch = newSketch(context, id + "F29", { "sketchPlane" : qUnion([Q0])});
            skLineSegment(sketch, "E46.bottom", {"start": v(-278.08, -13.13) * mm, "end": v(-287.6, -13.13) * mm});
            skLineSegment(sketch, "E46.top", {"start": v(-278.08, -63.93) * mm, "end": v(-287.6, -63.93) * mm});
            skLineSegment(sketch, "E46.left", {"start": v(-278.08, -13.13) * mm, "end": v(-278.08, -63.93) * mm});
            skLineSegment(sketch, "E46.right", {"start": v(-287.6, -13.13) * mm, "end": v(-287.6, -63.93) * mm});
            skLineSegment(sketch, "E47.1.0.0", {"start": v(-265.38, -13.13) * mm, "end": v(-274.9, -13.13) * mm});
            skLineSegment(sketch, "E47.1.0.1", {"start": v(-274.9, -13.13) * mm, "end": v(-274.9, -63.93) * mm});
            skLineSegment(sketch, "E47.1.0.2", {"start": v(-265.38, -13.13) * mm, "end": v(-265.38, -63.93) * mm});
            skLineSegment(sketch, "E47.1.0.3", {"start": v(-265.38, -63.93) * mm, "end": v(-274.9, -63.93) * mm});
            skLineSegment(sketch, "E47.2.0.0", {"start": v(-252.68, -13.13) * mm, "end": v(-262.2, -13.13) * mm});
            skLineSegment(sketch, "E47.2.0.1", {"start": v(-262.2, -13.13) * mm, "end": v(-262.2, -63.93) * mm});
            skLineSegment(sketch, "E47.2.0.2", {"start": v(-252.68, -13.13) * mm, "end": v(-252.68, -63.93) * mm});
            skLineSegment(sketch, "E47.2.0.3", {"start": v(-252.68, -63.93) * mm, "end": v(-262.2, -63.93) * mm});
            skLineSegment(sketch, "E47.3.0.0", {"start": v(-239.98, -13.13) * mm, "end": v(-249.5, -13.13) * mm});
            skLineSegment(sketch, "E47.3.0.1", {"start": v(-249.5, -13.13) * mm, "end": v(-249.5, -63.93) * mm});
            skLineSegment(sketch, "E47.3.0.2", {"start": v(-239.98, -13.13) * mm, "end": v(-239.98, -63.93) * mm});
            skLineSegment(sketch, "E47.3.0.3", {"start": v(-239.98, -63.93) * mm, "end": v(-249.5, -63.93) * mm});
            skLineSegment(sketch, "E47.4.0.0", {"start": v(-227.28, -13.13) * mm, "end": v(-236.8, -13.13) * mm});
            skLineSegment(sketch, "E47.4.0.1", {"start": v(-236.8, -13.13) * mm, "end": v(-236.8, -63.93) * mm});
            skLineSegment(sketch, "E47.4.0.2", {"start": v(-227.28, -13.13) * mm, "end": v(-227.28, -63.93) * mm});
            skLineSegment(sketch, "E47.4.0.3", {"start": v(-227.28, -63.93) * mm, "end": v(-236.8, -63.93) * mm});
            skLineSegment(sketch, "E47.direction1", {"start": v(-287.6, -13.13) * mm, "end": v(-274.9, -13.13) * mm, "construction": true});
            skLineSegment(sketch, "E48.bottom", {"start": v(-151.08, -13.52) * mm, "end": v(-160.6, -13.52) * mm});
            skLineSegment(sketch, "E48.top", {"start": v(-151.08, -64.32) * mm, "end": v(-160.6, -64.32) * mm});
            skLineSegment(sketch, "E48.left", {"start": v(-151.08, -13.52) * mm, "end": v(-151.08, -64.32) * mm});
            skLineSegment(sketch, "E48.right", {"start": v(-160.6, -13.52) * mm, "end": v(-160.6, -64.32) * mm});
            skLineSegment(sketch, "E49.1.0.0", {"start": v(-138.38, -13.52) * mm, "end": v(-147.9, -13.52) * mm});
            skLineSegment(sketch, "E49.1.0.1", {"start": v(-147.9, -13.52) * mm, "end": v(-147.9, -64.32) * mm});
            skLineSegment(sketch, "E49.1.0.2", {"start": v(-138.38, -13.52) * mm, "end": v(-138.38, -64.32) * mm});
            skLineSegment(sketch, "E49.1.0.3", {"start": v(-138.38, -64.32) * mm, "end": v(-147.9, -64.32) * mm});
            skLineSegment(sketch, "E49.2.0.0", {"start": v(-125.68, -13.52) * mm, "end": v(-135.2, -13.52) * mm});
            skLineSegment(sketch, "E49.2.0.1", {"start": v(-135.2, -13.52) * mm, "end": v(-135.2, -64.32) * mm});
            skLineSegment(sketch, "E49.2.0.2", {"start": v(-125.68, -13.52) * mm, "end": v(-125.68, -64.32) * mm});
            skLineSegment(sketch, "E49.2.0.3", {"start": v(-125.68, -64.32) * mm, "end": v(-135.2, -64.32) * mm});
            skLineSegment(sketch, "E49.3.0.0", {"start": v(-112.98, -13.52) * mm, "end": v(-122.5, -13.52) * mm});
            skLineSegment(sketch, "E49.3.0.1", {"start": v(-122.5, -13.52) * mm, "end": v(-122.5, -64.32) * mm});
            skLineSegment(sketch, "E49.3.0.2", {"start": v(-112.98, -13.52) * mm, "end": v(-112.98, -64.32) * mm});
            skLineSegment(sketch, "E49.3.0.3", {"start": v(-112.98, -64.32) * mm, "end": v(-122.5, -64.32) * mm});
            skLineSegment(sketch, "E49.4.0.0", {"start": v(-100.28, -13.52) * mm, "end": v(-109.8, -13.52) * mm});
            skLineSegment(sketch, "E49.4.0.1", {"start": v(-109.8, -13.52) * mm, "end": v(-109.8, -64.32) * mm});
            skLineSegment(sketch, "E49.4.0.2", {"start": v(-100.28, -13.52) * mm, "end": v(-100.28, -64.32) * mm});
            skLineSegment(sketch, "E49.4.0.3", {"start": v(-100.28, -64.32) * mm, "end": v(-109.8, -64.32) * mm});
            skLineSegment(sketch, "E49.direction1", {"start": v(-160.6, -13.52) * mm, "end": v(-147.9, -13.52) * mm, "construction": true});
            skLineSegment(sketch, "E50.bottom", {"start": v(-24.08, -11.03) * mm, "end": v(-33.6, -11.03) * mm});
            skLineSegment(sketch, "E50.top", {"start": v(-24.08, -61.83) * mm, "end": v(-33.6, -61.83) * mm});
            skLineSegment(sketch, "E50.left", {"start": v(-24.08, -11.03) * mm, "end": v(-24.08, -61.83) * mm});
            skLineSegment(sketch, "E50.right", {"start": v(-33.6, -11.03) * mm, "end": v(-33.6, -61.83) * mm});
            skLineSegment(sketch, "E51.1.0.0", {"start": v(-11.38, -11.03) * mm, "end": v(-20.9, -11.03) * mm});
            skLineSegment(sketch, "E51.1.0.1", {"start": v(-20.9, -11.03) * mm, "end": v(-20.9, -61.83) * mm});
            skLineSegment(sketch, "E51.1.0.2", {"start": v(-11.38, -11.03) * mm, "end": v(-11.38, -61.83) * mm});
            skLineSegment(sketch, "E51.1.0.3", {"start": v(-11.38, -61.83) * mm, "end": v(-20.9, -61.83) * mm});
            skLineSegment(sketch, "E51.2.0.0", {"start": v(1.32, -11.03) * mm, "end": v(-8.2, -11.03) * mm});
            skLineSegment(sketch, "E51.2.0.1", {"start": v(-8.2, -11.03) * mm, "end": v(-8.2, -61.83) * mm});
            skLineSegment(sketch, "E51.2.0.2", {"start": v(1.32, -11.03) * mm, "end": v(1.32, -61.83) * mm});
            skLineSegment(sketch, "E51.2.0.3", {"start": v(1.32, -61.83) * mm, "end": v(-8.2, -61.83) * mm});
            skLineSegment(sketch, "E51.3.0.0", {"start": v(14.02, -11.03) * mm, "end": v(4.5, -11.03) * mm});
            skLineSegment(sketch, "E51.3.0.1", {"start": v(4.5, -11.03) * mm, "end": v(4.5, -61.83) * mm});
            skLineSegment(sketch, "E51.3.0.2", {"start": v(14.02, -11.03) * mm, "end": v(14.02, -61.83) * mm});
            skLineSegment(sketch, "E51.3.0.3", {"start": v(14.02, -61.83) * mm, "end": v(4.5, -61.83) * mm});
            skLineSegment(sketch, "E51.4.0.0", {"start": v(26.72, -11.03) * mm, "end": v(17.2, -11.03) * mm});
            skLineSegment(sketch, "E51.4.0.1", {"start": v(17.2, -11.03) * mm, "end": v(17.2, -61.83) * mm});
            skLineSegment(sketch, "E51.4.0.2", {"start": v(26.72, -11.03) * mm, "end": v(26.72, -61.83) * mm});
            skLineSegment(sketch, "E51.4.0.3", {"start": v(26.72, -61.83) * mm, "end": v(17.2, -61.83) * mm});
            skLineSegment(sketch, "E51.direction1", {"start": v(-33.6, -11.03) * mm, "end": v(-20.9, -11.03) * mm, "construction": true});
            skLineSegment(sketch, "E52.bottom", {"start": v(102.92, -15.38) * mm, "end": v(93.4, -15.38) * mm});
            skLineSegment(sketch, "E52.top", {"start": v(102.92, -66.18) * mm, "end": v(93.4, -66.18) * mm});
            skLineSegment(sketch, "E52.left", {"start": v(102.92, -15.38) * mm, "end": v(102.92, -66.18) * mm});
            skLineSegment(sketch, "E52.right", {"start": v(93.4, -15.38) * mm, "end": v(93.4, -66.18) * mm});
            skLineSegment(sketch, "E53.1.0.0", {"start": v(115.62, -15.38) * mm, "end": v(106.1, -15.38) * mm});
            skLineSegment(sketch, "E53.1.0.1", {"start": v(106.1, -15.38) * mm, "end": v(106.1, -66.18) * mm});
            skLineSegment(sketch, "E53.1.0.2", {"start": v(115.62, -15.38) * mm, "end": v(115.62, -66.18) * mm});
            skLineSegment(sketch, "E53.1.0.3", {"start": v(115.62, -66.18) * mm, "end": v(106.1, -66.18) * mm});
            skLineSegment(sketch, "E53.2.0.0", {"start": v(128.32, -15.38) * mm, "end": v(118.8, -15.38) * mm});
            skLineSegment(sketch, "E53.2.0.1", {"start": v(118.8, -15.38) * mm, "end": v(118.8, -66.18) * mm});
            skLineSegment(sketch, "E53.2.0.2", {"start": v(128.32, -15.38) * mm, "end": v(128.32, -66.18) * mm});
            skLineSegment(sketch, "E53.2.0.3", {"start": v(128.32, -66.18) * mm, "end": v(118.8, -66.18) * mm});
            skLineSegment(sketch, "E53.3.0.0", {"start": v(141.02, -15.38) * mm, "end": v(131.5, -15.38) * mm});
            skLineSegment(sketch, "E53.3.0.1", {"start": v(131.5, -15.38) * mm, "end": v(131.5, -66.18) * mm});
            skLineSegment(sketch, "E53.3.0.2", {"start": v(141.02, -15.38) * mm, "end": v(141.02, -66.18) * mm});
            skLineSegment(sketch, "E53.3.0.3", {"start": v(141.02, -66.18) * mm, "end": v(131.5, -66.18) * mm});
            skLineSegment(sketch, "E53.4.0.0", {"start": v(153.72, -15.38) * mm, "end": v(144.2, -15.38) * mm});
            skLineSegment(sketch, "E53.4.0.1", {"start": v(144.2, -15.38) * mm, "end": v(144.2, -66.18) * mm});
            skLineSegment(sketch, "E53.4.0.2", {"start": v(153.72, -15.38) * mm, "end": v(153.72, -66.18) * mm});
            skLineSegment(sketch, "E53.4.0.3", {"start": v(153.72, -66.18) * mm, "end": v(144.2, -66.18) * mm});
            skLineSegment(sketch, "E53.direction1", {"start": v(93.4, -15.38) * mm, "end": v(106.1, -15.38) * mm, "construction": true});
            skLineSegment(sketch, "E54.bottom", {"start": v(227.38, -13.94) * mm, "end": v(217.85, -13.94) * mm});
            skLineSegment(sketch, "E54.top", {"start": v(227.38, -64.74) * mm, "end": v(217.85, -64.74) * mm});
            skLineSegment(sketch, "E54.left", {"start": v(227.38, -13.94) * mm, "end": v(227.38, -64.74) * mm});
            skLineSegment(sketch, "E54.right", {"start": v(217.85, -13.94) * mm, "end": v(217.85, -64.74) * mm});
            skLineSegment(sketch, "E55.1.0.0", {"start": v(240.08, -13.94) * mm, "end": v(230.55, -13.94) * mm});
            skLineSegment(sketch, "E55.1.0.1", {"start": v(230.55, -13.94) * mm, "end": v(230.55, -64.74) * mm});
            skLineSegment(sketch, "E55.1.0.2", {"start": v(240.08, -13.94) * mm, "end": v(240.08, -64.74) * mm});
            skLineSegment(sketch, "E55.1.0.3", {"start": v(240.08, -64.74) * mm, "end": v(230.55, -64.74) * mm});
            skLineSegment(sketch, "E55.2.0.0", {"start": v(252.78, -13.94) * mm, "end": v(243.25, -13.94) * mm});
            skLineSegment(sketch, "E55.2.0.1", {"start": v(243.25, -13.94) * mm, "end": v(243.25, -64.74) * mm});
            skLineSegment(sketch, "E55.2.0.2", {"start": v(252.78, -13.94) * mm, "end": v(252.78, -64.74) * mm});
            skLineSegment(sketch, "E55.2.0.3", {"start": v(252.78, -64.74) * mm, "end": v(243.25, -64.74) * mm});
            skLineSegment(sketch, "E55.3.0.0", {"start": v(265.48, -13.94) * mm, "end": v(255.95, -13.94) * mm});
            skLineSegment(sketch, "E55.3.0.1", {"start": v(255.95, -13.94) * mm, "end": v(255.95, -64.74) * mm});
            skLineSegment(sketch, "E55.3.0.2", {"start": v(265.48, -13.94) * mm, "end": v(265.48, -64.74) * mm});
            skLineSegment(sketch, "E55.3.0.3", {"start": v(265.48, -64.74) * mm, "end": v(255.95, -64.74) * mm});
            skLineSegment(sketch, "E55.4.0.0", {"start": v(278.18, -13.94) * mm, "end": v(268.65, -13.94) * mm});
            skLineSegment(sketch, "E55.4.0.1", {"start": v(268.65, -13.94) * mm, "end": v(268.65, -64.74) * mm});
            skLineSegment(sketch, "E55.4.0.2", {"start": v(278.18, -13.94) * mm, "end": v(278.18, -64.74) * mm});
            skLineSegment(sketch, "E55.4.0.3", {"start": v(278.18, -64.74) * mm, "end": v(268.65, -64.74) * mm});
            skLineSegment(sketch, "E55.direction1", {"start": v(217.85, -13.94) * mm, "end": v(230.55, -13.94) * mm, "construction": true});
            skSolve(sketch);
        }
        {
            var Q0;
            Q0 = qSketchRegion(id + "F29", true);
            extrude(context, id + "F30", {"entities" : qUnion([Q0]), "operationType" : NewBodyOperationType.REMOVE, "endBound" : BoundingType.THROUGH_ALL, "oppositeDirection" : true, "depth" : 25.4 * mm});
        }
        {
            var Q0;
            Q0=makeQuery(id+"F28.opExtrude","SWEPT_EDGE",EDGE,{"disambiguationData":[OSD([sQuery(id+"F27.wireOp",EDGE,"E39.bottom"),sQuery(id+"F27.wireOp",EDGE,"E39.left")])]});
            var Q1;
            Q1=makeQuery(id+"F28.opExtrude","SWEPT_EDGE",EDGE,{"disambiguationData":[OSD([sQuery(id+"F27.wireOp",EDGE,"E39.top"),sQuery(id+"F27.wireOp",EDGE,"E39.left")])]});
            var Q2;
            Q2=makeQuery(id+"F28.opExtrude","SWEPT_EDGE",EDGE,{"disambiguationData":[OSD([sQuery(id+"F27.wireOp",EDGE,"E39.bottom"),sQuery(id+"F27.wireOp",EDGE,"E39.right")])]});
            var Q3;
            Q3=makeQuery(id+"F28.opExtrude","SWEPT_EDGE",EDGE,{"disambiguationData":[OSD([sQuery(id+"F27.wireOp",EDGE,"E39.top"),sQuery(id+"F27.wireOp",EDGE,"E39.right")])]});
            fillet(context, id + "F31", {"entities" : qUnion([Q0, Q1, Q2, Q3]), "radius" : 12.7 * mm, "tangentPropagation" : true, "allowEdgeOverflow" : false});
        }
        {
            var Q0;
            Q0=makeQuery(id+"F28.opExtrude","CAP_EDGE",EDGE,{"disambiguationData":[OSD([sQuery(id+"F27.wireOp",EDGE,"E39.bottom")])],"isStart":false});
            var Q1;
            Q1=makeQuery(id+"F28.opExtrude","CAP_EDGE",EDGE,{"disambiguationData":[OSD([sQuery(id+"F27.wireOp",EDGE,"E39.bottom")])],"isStart":true});
            fillet(context, id + "F32", {"entities" : qUnion([Q0, Q1]), "radius" : 1.6 * mm, "tangentPropagation" : true, "allowEdgeOverflow" : false});
        }
    });
